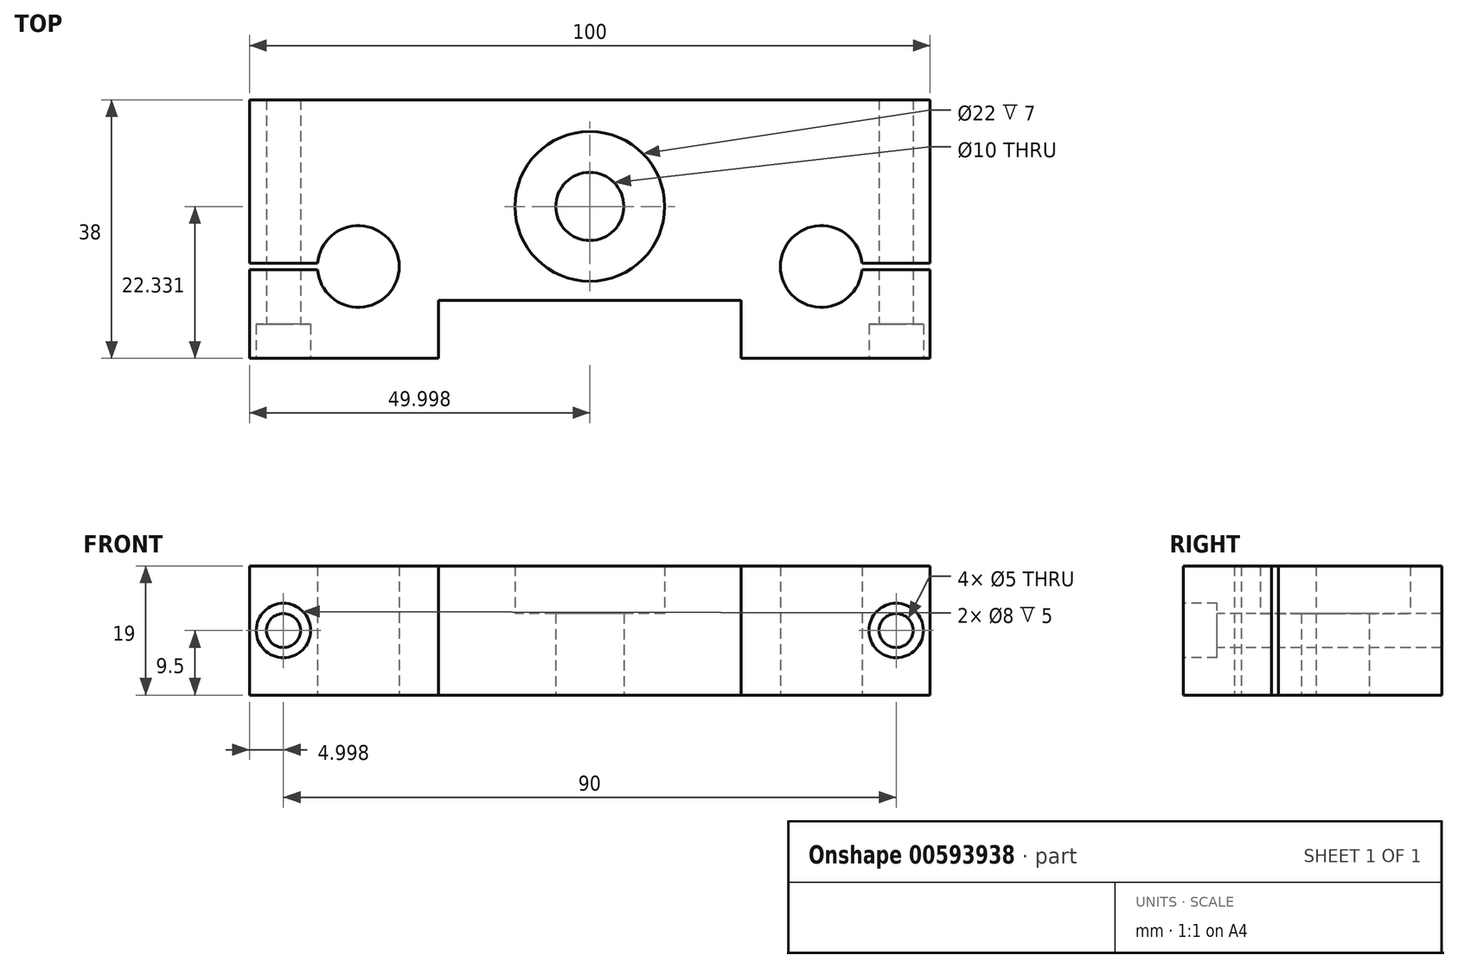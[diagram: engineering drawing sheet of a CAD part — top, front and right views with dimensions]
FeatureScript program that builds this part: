
annotation { "Feature Type Name" : "Feature", "Feature Type Description" : "" }
export const myFeature = defineFeature(function(context is Context, id is Id, definition is map)
    precondition{}
    {
        {
            var Q0;
            Q0=qCreatedBy(makeId("Top.planeOp"),FACE);
            var sketch = newSketch(context, id + "F0", { "sketchPlane" : qUnion([Q0])});
            skLineSegment(sketch, "E0.bottom", {"start": v(-90.61, -2.98) * mm, "end": v(9.39, -2.98) * mm});
            skLineSegment(sketch, "E0.top", {"start": v(-90.61, -40.98) * mm, "end": v(9.39, -40.98) * mm});
            skLineSegment(sketch, "E0.left", {"start": v(-90.61, -2.98) * mm, "end": v(-90.61, -40.98) * mm});
            skLineSegment(sketch, "E0.right", {"start": v(9.39, -2.98) * mm, "end": v(9.39, -40.98) * mm});
            skCircle(sketch, "E1", {"center": v(-74.61, -27.48) * mm, "radius": 6 * mm});
            skCircle(sketch, "E2", {"center": v(-6.61, -27.48) * mm, "radius": 6 * mm});
            skCircle(sketch, "E3", {"center": v(-40.61, -18.65) * mm, "radius": 11 * mm});
            skPoint(sketch, "E3.centerSnap0", {"position": v(-40.61, -2.98) * mm});
            skCircle(sketch, "E4", {"center": v(-40.61, -18.65) * mm, "radius": 5 * mm});
            skLineSegment(sketch, "E5.bottom", {"start": v(-6.61, -26.98) * mm, "end": v(9.39, -26.98) * mm});
            skLineSegment(sketch, "E5.top", {"start": v(-6.61, -27.98) * mm, "end": v(9.39, -27.98) * mm});
            skLineSegment(sketch, "E5.left", {"start": v(-6.61, -26.98) * mm, "end": v(-6.61, -27.98) * mm});
            skLineSegment(sketch, "E5.right", {"start": v(9.39, -26.98) * mm, "end": v(9.39, -27.98) * mm});
            skLineSegment(sketch, "E6.bottom", {"start": v(-74.61, -26.98) * mm, "end": v(-90.61, -26.98) * mm});
            skLineSegment(sketch, "E6.top", {"start": v(-74.61, -27.98) * mm, "end": v(-90.61, -27.98) * mm});
            skLineSegment(sketch, "E6.left", {"start": v(-74.61, -26.98) * mm, "end": v(-74.61, -27.98) * mm});
            skLineSegment(sketch, "E6.right", {"start": v(-90.61, -26.98) * mm, "end": v(-90.61, -27.98) * mm});
            skLineSegment(sketch, "E7.bottom", {"start": v(-18.4, -32.45) * mm, "end": v(-62.83, -32.45) * mm});
            skLineSegment(sketch, "E7.top", {"start": v(-18.4, -46.3) * mm, "end": v(-62.83, -46.3) * mm});
            skLineSegment(sketch, "E7.left", {"start": v(-18.4, -32.45) * mm, "end": v(-18.4, -46.3) * mm});
            skLineSegment(sketch, "E7.right", {"start": v(-62.83, -32.45) * mm, "end": v(-62.83, -46.3) * mm});
            skPoint(sketch, "E7.middle", {"position": v(-40.61, -40.98) * mm});
            skSolve(sketch);
        }
        {
            var Q0;
            Q0=makeQuery(id+"F0.imprint","IMPRINT",FACE,{"disambiguationData":[TD([[makeQuery(id+"F0.imprint","IMPRINT",EDGE,{"derivedFrom":sQuery(id+"F0.wireOp",EDGE,"E0.bottom")}),-1.0]])]});
            extrude(context, id + "F1", {"entities" : qUnion([Q0]), "depth" : 19 * mm, "offsetDistance" : 25 * mm});
        }
        {
            var Q0;
            Q0=makeQuery(id+"F0.imprint","IMPRINT",FACE,{"disambiguationData":[TD([[makeQuery(id+"F0.imprint","IMPRINT",EDGE,{"derivedFrom":sQuery(id+"F0.wireOp",EDGE,"E3")}),1.0]])]});
            extrude(context, id + "F2", {"entities" : qUnion([Q0]), "operationType" : NewBodyOperationType.ADD, "depth" : 12 * mm, "offsetDistance" : 25 * mm});
        }
        {
            var Q0;
            Q0=makeQuery(id+"F1.opExtrude","SWEPT_FACE",FACE,{"disambiguationData":[OSD([sQuery(id+"F0.wireOp",EDGE,"E0.top")])]});
            var sketch = newSketch(context, id + "F3", { "sketchPlane" : qUnion([Q0])});
            skCircle(sketch, "E8", {"center": v(-85.61, 9.5) * mm, "radius": 2.5 * mm});
            skPoint(sketch, "E8.centerSnap0", {"position": v(-90.61, 9.5) * mm});
            skCircle(sketch, "E9", {"center": v(-85.61, 9.5) * mm, "radius": 4 * mm});
            skCircle(sketch, "E10.1.0.0", {"center": v(4.39, 9.5) * mm, "radius": 4 * mm});
            skCircle(sketch, "E10.1.0.1", {"center": v(4.39, 9.5) * mm, "radius": 2.5 * mm});
            skSolve(sketch);
        }
        {
            var Q0;
            Q0=makeQuery(id+"F3.imprint","IMPRINT",FACE,{"disambiguationData":[TD([[makeQuery(id+"F3.imprint","IMPRINT",EDGE,{"derivedFrom":sQuery(id+"F3.wireOp",EDGE,"E8")}),1.0]])]});
            var Q1;
            Q1=makeQuery(id+"F3.imprint","IMPRINT",FACE,{"disambiguationData":[TD([[makeQuery(id+"F3.imprint","IMPRINT",EDGE,{"derivedFrom":sQuery(id+"F3.wireOp",EDGE,"E10.1.0.1")}),1.0]])]});
            extrude(context, id + "F4", {"entities" : qUnion([Q0, Q1]), "operationType" : NewBodyOperationType.REMOVE, "endBound" : BoundingType.THROUGH_ALL, "oppositeDirection" : true, "depth" : 25 * mm, "offsetDistance" : 25 * mm});
        }
        {
            var Q0;
            Q0=makeQuery(id+"F3.imprint","IMPRINT",FACE,{"disambiguationData":[TD([[makeQuery(id+"F3.imprint","IMPRINT",EDGE,{"derivedFrom":sQuery(id+"F3.wireOp",EDGE,"E8")}),-1.0]])]});
            var Q1;
            Q1=makeQuery(id+"F3.imprint","IMPRINT",FACE,{"disambiguationData":[TD([[makeQuery(id+"F3.imprint","IMPRINT",EDGE,{"derivedFrom":sQuery(id+"F3.wireOp",EDGE,"E10.1.0.0")}),1.0]])]});
            extrude(context, id + "F5", {"entities" : qUnion([Q0, Q1]), "operationType" : NewBodyOperationType.REMOVE, "oppositeDirection" : true, "depth" : 5 * mm, "offsetDistance" : 25 * mm});
        }
    });
